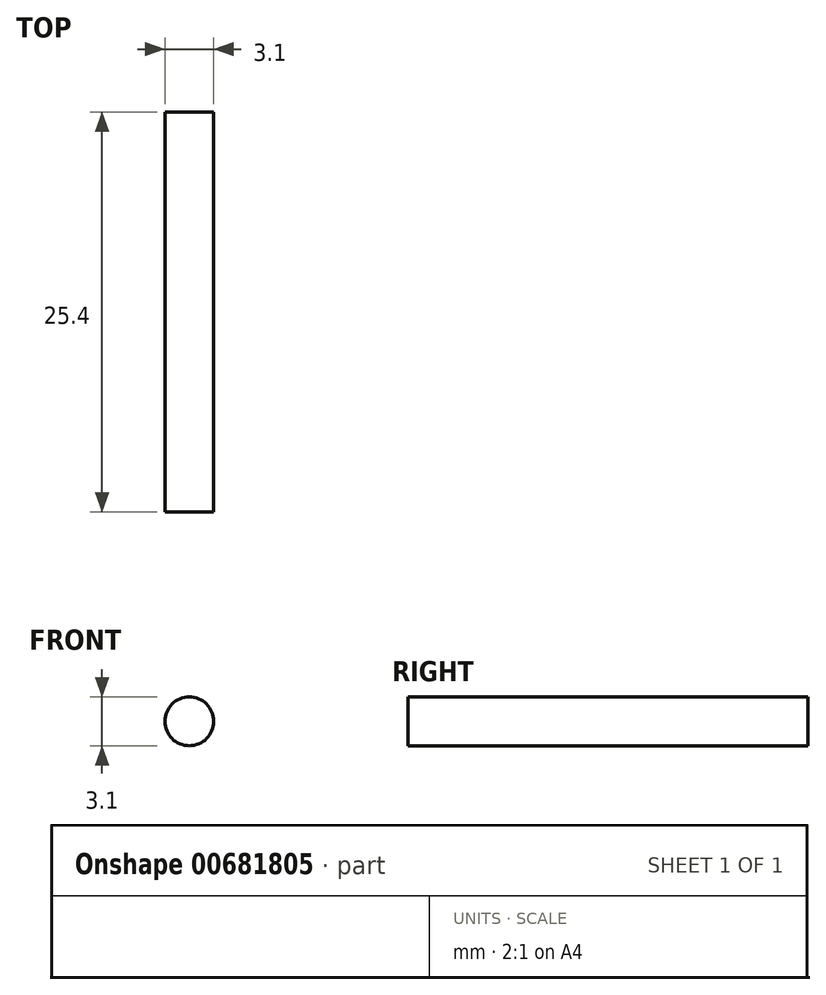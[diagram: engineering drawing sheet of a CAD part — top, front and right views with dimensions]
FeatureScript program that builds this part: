
annotation { "Feature Type Name" : "Feature", "Feature Type Description" : "" }
export const myFeature = defineFeature(function(context is Context, id is Id, definition is map)
    precondition{}
    {
        {
            var Q0;
            Q0=qCreatedBy(makeId("Front.planeOp"),FACE);
            var sketch = newSketch(context, id + "F0", { "sketchPlane" : qUnion([Q0])});
            skCircle(sketch, "E0", {"center": v(-32.94, 21.86) * mm, "radius": 1.55 * mm});
            skSolve(sketch);
        }
        {
            var Q0;
            Q0 = qSketchRegion(id + "F0", true);
            extrude(context, id + "F1", {"entities" : qUnion([Q0]), "depth" : 25.4 * mm, "offsetDistance" : 25.4 * mm});
        }
    });
